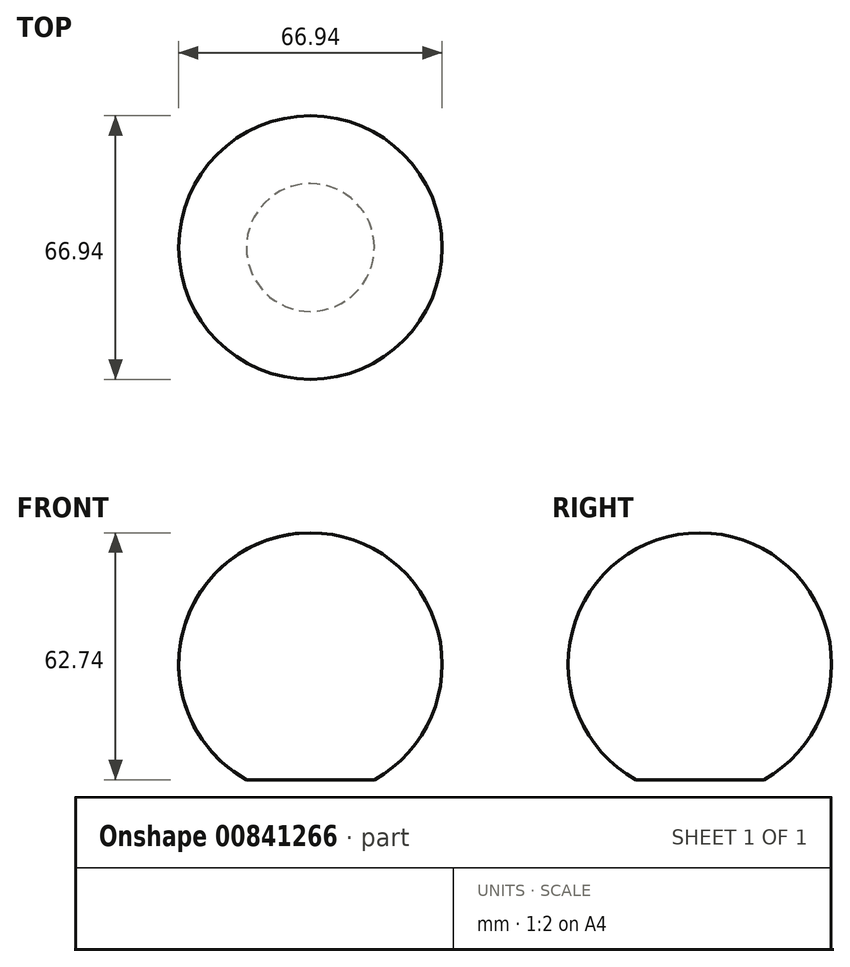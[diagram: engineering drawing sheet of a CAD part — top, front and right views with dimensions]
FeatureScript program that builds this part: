
annotation { "Feature Type Name" : "Feature", "Feature Type Description" : "" }
export const myFeature = defineFeature(function(context is Context, id is Id, definition is map)
    precondition{}
    {
        {
            var Q0;
            Q0=qCreatedBy(makeId("Front.planeOp"),FACE);
            var sketch = newSketch(context, id + "F0", { "sketchPlane" : qUnion([Q0])});
            skCircle(sketch, "E0", {"center": v(0, 0) * mm, "radius": 33.47 * mm});
            skLineSegment(sketch, "E1", {"start": v(-16.24, -29.27) * mm, "end": v(0, -29.27) * mm});
            skLineSegment(sketch, "E2", {"start": v(0, -29.27) * mm, "end": v(0, 33.47) * mm});
            skSolve(sketch);
        }
        {
            var Q0;
            {var subQ0=sQuery(id+"F0.wireOp",EDGE,"E1");Q0=makeQuery(id+"F0.imprint","IMPRINT",FACE,{"disambiguationData":[TD([[makeQuery(id+"F0.imprint","IMPRINT",EDGE,{"derivedFrom":subQ0}),1.0]])]});}
            var Q1;
            Q1=sQuery(id+"F0.wireOp",EDGE,"E2");
            revolve(context, id + "F1", {"surfaceOperationType" : NewSurfaceOperationType.NEW, "entities" : qUnion([Q0]), "axis" : qUnion([Q1]), "revolveType" : RevolveType.FULL});
        }
    });
